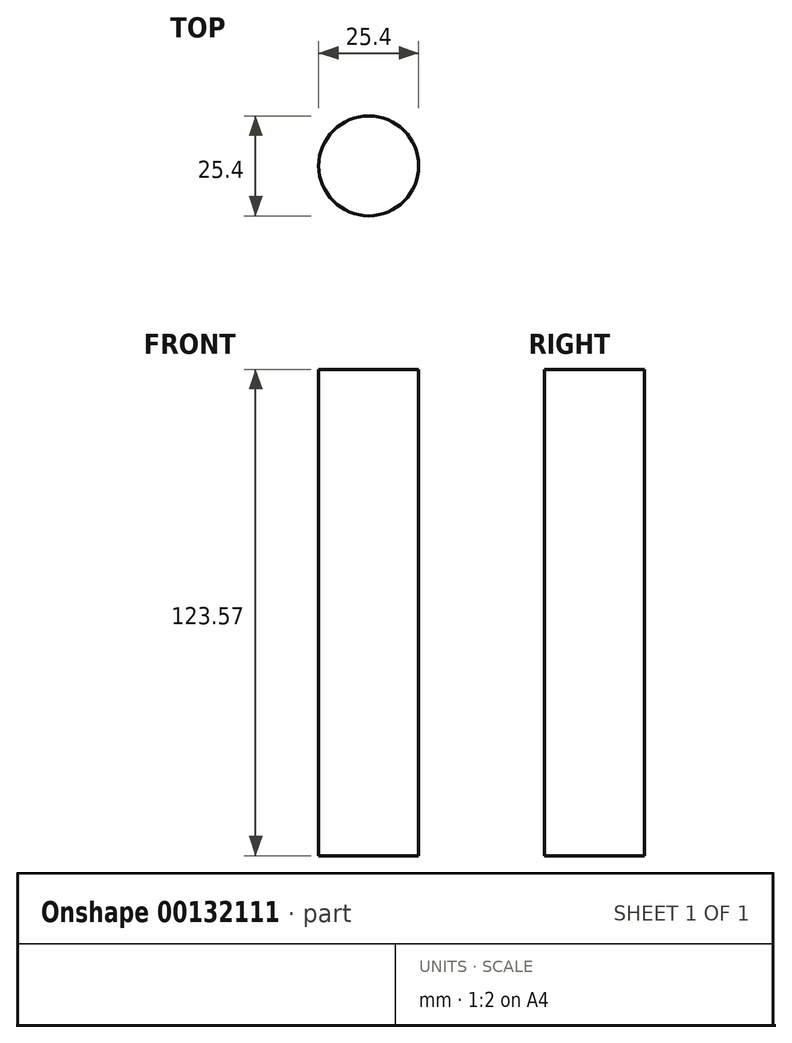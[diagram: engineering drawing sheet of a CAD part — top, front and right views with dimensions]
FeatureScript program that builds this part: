
annotation { "Feature Type Name" : "Feature", "Feature Type Description" : "" }
export const myFeature = defineFeature(function(context is Context, id is Id, definition is map)
    precondition{}
    {
        {
            var Q0;
            Q0=qCreatedBy(makeId("Top.planeOp"),FACE);
            var sketch = newSketch(context, id + "F0", { "sketchPlane" : qUnion([Q0])});
            skCircle(sketch, "E0", {"center": v(0, 0) * mm, "radius": 12.7 * mm});
            skSolve(sketch);
        }
        {
            var Q0;
            Q0=makeQuery(id+"F0.imprint","IMPRINT",FACE,{"disambiguationData":[TD([[makeQuery(id+"F0.imprint","IMPRINT",EDGE,{"derivedFrom":sQuery(id+"F0.wireOp",EDGE,"E0")}),1.0]])]});
            extrude(context, id + "F1", {"entities" : qUnion([Q0]), "depth" : 123.57 * mm});
        }
    });
